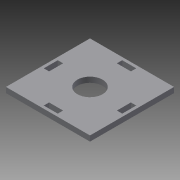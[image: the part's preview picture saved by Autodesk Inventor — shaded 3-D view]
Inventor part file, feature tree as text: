
AUTODESK INVENTOR PART (.ipt)
format: ipt  version: 2015 SP1 (Build 190203100, 203)  size: 110,592 bytes
history: native  units: in
note: dims shown in document units (in); Inventor stores cm internally (conversion verified against a paired STEP export)
features: extrude x1, sketch x1
ambient origin geometry x8: Origin, YZ Plane, XZ Plane, XY Plane, X Axis, Y Axis, Z Axis, Center Point
bodies: Body1 (feature_tree)
feature tree (2):
  extrude  "Extrusion3"  Depth=3.0in
  sketch  "Sketch1"  dims[d0=3.0in d1=3.0in d6=1.25in d7=0.1in d8=0.19in d9=0.5in d15=1.25in d16=0.5in d17=0.19in d18=0.9in d19=0.19in d20=0.0in]
